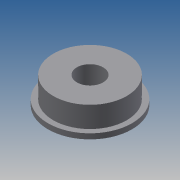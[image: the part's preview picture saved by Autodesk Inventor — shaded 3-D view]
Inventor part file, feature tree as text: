
AUTODESK INVENTOR PART (.ipt)
format: ipt  version: 2013 (Build 170138000, 138)  size: 86,528 bytes
history: native  units: mm
features: extrude x3, sketch x3
ambient origin geometry x8: Origin, YZ Plane, XZ Plane, XY Plane, X Axis, Y Axis, Z Axis, Center Point
bodies: Solid1 (feature_tree)
feature tree (6):
  extrude  "Extrusion1"  Depth=1.0mm TaperAngle=0.0deg
  extrude  "Extrusion2"  Depth=4.0mm TaperAngle=0.0deg
  extrude  "Extrusion3"  Depth=4.0mm TaperAngle=0.0deg
  sketch  "Sketch1"  dims[d0=16.0mm d2=1.0mm d3=0.0mm]
  sketch  "Sketch2"  dims[d4=14.0mm d6=4.0mm d7=0.0mm]
  sketch  "Sketch3"  dims[d8=5.0mm d10=4.0mm d11=0.0mm]
